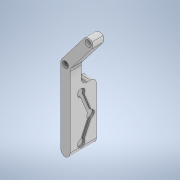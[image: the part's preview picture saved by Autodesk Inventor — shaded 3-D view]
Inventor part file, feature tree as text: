
AUTODESK INVENTOR PART (.ipt)
format: ipt  version: 2022 (Build 260153000, 153)  size: 185,856 bytes
history: native  units: in
note: dims shown in document units (in); Inventor stores cm internally (conversion verified against a paired STEP export)
features: extrude x3, sketch x3, fillet x2, projected_geometry x2
ambient origin geometry x8: Origin, YZ Plane, XZ Plane, XY Plane, X Axis, Y Axis, Z Axis, Center Point
bodies: Solid1 (feature_tree)
feature tree (10):
  extrude  "Extrusion1"  Depth=0.794in
  fillet  "Fillet1"  Radius=0.3607in
  extrude  "Extrusion2"  Depth=0.13in
  fillet  "Fillet2"  Radius=0.1in
  extrude  "Extrusion3"  Depth=0.125in
  sketch  "Sketch1"  dims[d0=1.7in d1=0.794in d2=0.3607in]
  sketch  "Sketch2"  dims[d3=0.13in d4=0.13in d5=0.1in]
  projected_geometry  "Projected Loop1"
  sketch  "Sketch3"  dims[d6=0.1in d7=0.125in d8=0.233in d9=0.0in d10=0.125in d11=1.25in d12=0.325in d13=0.0in d14=0.125in d15=0.1575in d16=0.1575in d17=0.1575in d18=0.0394in d19=0.0394in d20=0.0394in d21=0.0in]
  projected_geometry  "Projected Loop2"
